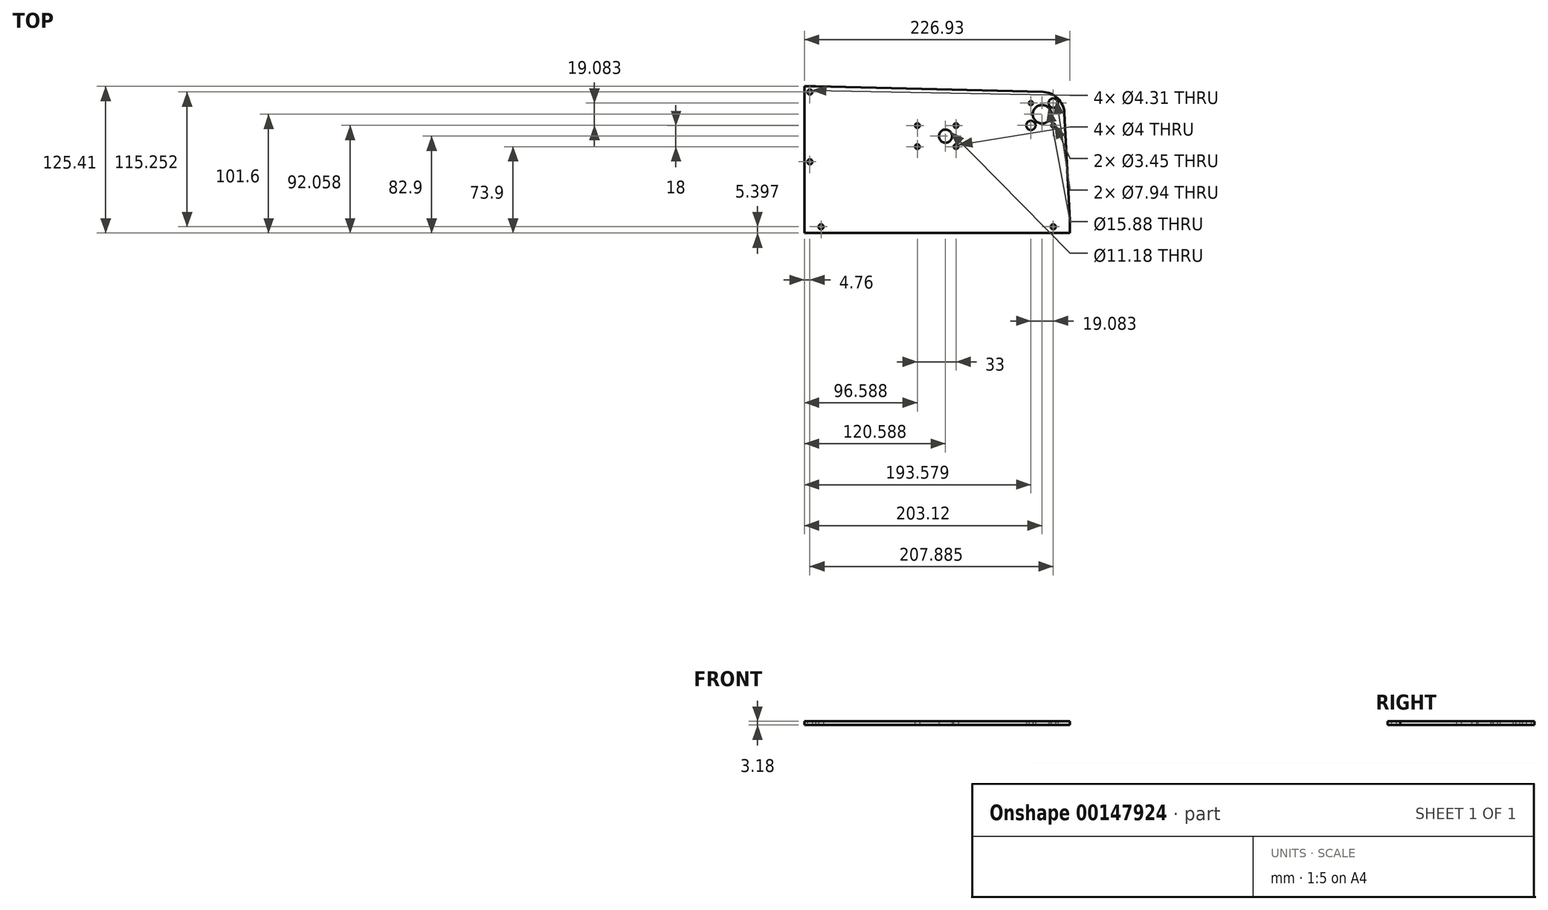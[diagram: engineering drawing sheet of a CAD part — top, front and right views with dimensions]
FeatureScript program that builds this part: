
annotation { "Feature Type Name" : "Feature", "Feature Type Description" : "" }
export const myFeature = defineFeature(function(context is Context, id is Id, definition is map)
    precondition{}
    {
        {
            var Q0;
            Q0=qCreatedBy(makeId("Top.planeOp"),FACE);
            var sketch = newSketch(context, id + "F0", { "sketchPlane" : qUnion([Q0])});
            skCircle(sketch, "E0", {"center": v(0, 0) * mm, "radius": 7.94 * mm});
            skCircle(sketch, "E1", {"center": v(-9.54, 9.54) * mm, "radius": 5.56 * mm, "construction": true});
            skCircle(sketch, "E2", {"center": v(-9.54, 9.54) * mm, "radius": 1.73 * mm});
            skCircle(sketch, "E3", {"center": v(9.54, -9.54) * mm, "radius": 1.73 * mm});
            skLineSegment(sketch, "E4.bottom", {"start": v(-193.6, 23.81) * mm, "end": v(0.47, 19.04) * mm});
            skLineSegment(sketch, "E4.top", {"start": v(-203.12, -101.6) * mm, "end": v(23.81, -101.6) * mm});
            skLineSegment(sketch, "E4.left", {"start": v(-203.12, 23.81) * mm, "end": v(-203.12, -101.6) * mm});
            skLineSegment(sketch, "E5.bottom", {"start": v(-9.54, 9.54) * mm, "end": v(9.54, 9.54) * mm, "construction": true});
            skLineSegment(sketch, "E5.top", {"start": v(-9.54, -9.54) * mm, "end": v(9.54, -9.54) * mm, "construction": true});
            skLineSegment(sketch, "E5.left", {"start": v(-9.54, 9.54) * mm, "end": v(-9.54, -9.54) * mm, "construction": true});
            skLineSegment(sketch, "E5.right", {"start": v(9.54, 9.54) * mm, "end": v(9.54, -9.54) * mm, "construction": true});
            skCircle(sketch, "E6", {"center": v(-9.54, -9.54) * mm, "radius": 3.97 * mm});
            skCircle(sketch, "E7", {"center": v(9.54, 9.54) * mm, "radius": 3.97 * mm});
            skArc(sketch, "E8", {"start": v(19.02, 1) * mm, "mid": v(13.28, 13.65) * mm, "end": v(0.47, 19.04) * mm});
            skLineSegment(sketch, "E9", {"start": v(23.81, -101.6) * mm, "end": v(23.81, -90.8) * mm});
            skLineSegment(sketch, "E10", {"start": v(23.81, -90.8) * mm, "end": v(19.02, 1) * mm});
            skLineSegment(sketch, "E11", {"start": v(0, 0) * mm, "end": v(0, -101.6) * mm, "construction": true});
            skLineSegment(sketch, "E12", {"start": v(23.81, -96.2) * mm, "end": v(9.53, -96.2) * mm, "construction": true});
            skCircle(sketch, "E13", {"center": v(9.53, -96.2) * mm, "radius": 2.15 * mm});
            skLineSegment(sketch, "E14", {"start": v(23.81, -90.8) * mm, "end": v(0, -90.8) * mm, "construction": true});
            skLineSegment(sketch, "E15", {"start": v(-203.12, 23.81) * mm, "end": v(-193.6, 23.81) * mm});
            skLineSegment(sketch, "E16", {"start": v(-198.36, 23.81) * mm, "end": v(-198.36, 19.05) * mm, "construction": true});
            skLineSegment(sketch, "E17", {"start": v(-203.12, -96.2) * mm, "end": v(-188.83, -96.2) * mm, "construction": true});
            skCircle(sketch, "E18", {"center": v(-188.83, -96.2) * mm, "radius": 2.15 * mm});
            skCircle(sketch, "E19", {"center": v(-198.36, 19.05) * mm, "radius": 2.15 * mm});
            skLineSegment(sketch, "E20", {"start": v(0, 0) * mm, "end": v(-198.36, 0) * mm, "construction": true});
            skLineSegment(sketch, "E21", {"start": v(-198.36, 0) * mm, "end": v(-198.36, 19.05) * mm, "construction": true});
            skLineSegment(sketch, "E22", {"start": v(-198.36, 0) * mm, "end": v(-198.36, -40.65) * mm, "construction": true});
            skLineSegment(sketch, "E23", {"start": v(-198.36, -40.65) * mm, "end": v(-198.36, -96.2) * mm, "construction": true});
            skCircle(sketch, "E24", {"center": v(-198.36, -40.65) * mm, "radius": 2.15 * mm});
            skLineSegment(sketch, "E25", {"start": v(0, 0) * mm, "end": v(-73.53, -18.7) * mm, "construction": true});
            skPoint(sketch, "E26.middle", {"position": v(-73.53, -18.7) * mm});
            skLineSegment(sketch, "E27.bottom", {"start": v(-73.53, -27.7) * mm, "end": v(-106.53, -27.7) * mm, "construction": true});
            skLineSegment(sketch, "E27.top", {"start": v(-73.53, -9.7) * mm, "end": v(-106.53, -9.7) * mm, "construction": true});
            skLineSegment(sketch, "E27.left", {"start": v(-73.53, -27.7) * mm, "end": v(-73.53, -9.7) * mm, "construction": true});
            skLineSegment(sketch, "E27.right", {"start": v(-106.53, -27.7) * mm, "end": v(-106.53, -9.7) * mm, "construction": true});
            skLineSegment(sketch, "E28", {"start": v(-82.53, -18.7) * mm, "end": v(-73.53, -18.7) * mm, "construction": true});
            skCircle(sketch, "E29", {"center": v(-106.53, -9.7) * mm, "radius": 2 * mm});
            skCircle(sketch, "E30", {"center": v(-106.53, -27.7) * mm, "radius": 2 * mm});
            skCircle(sketch, "E31", {"center": v(-73.53, -27.7) * mm, "radius": 2 * mm});
            skCircle(sketch, "E32", {"center": v(-73.53, -9.7) * mm, "radius": 2 * mm});
            skCircle(sketch, "E33", {"center": v(-82.53, -18.7) * mm, "radius": 5.59 * mm});
            skSolve(sketch);
        }
        {
            var Q0;
            Q0=qSketchRegion(id+"F0",true);
            extrude(context, id + "F1", {"entities" : qUnion([Q0]), "depth" : 3.17 * mm});
        }
    });
